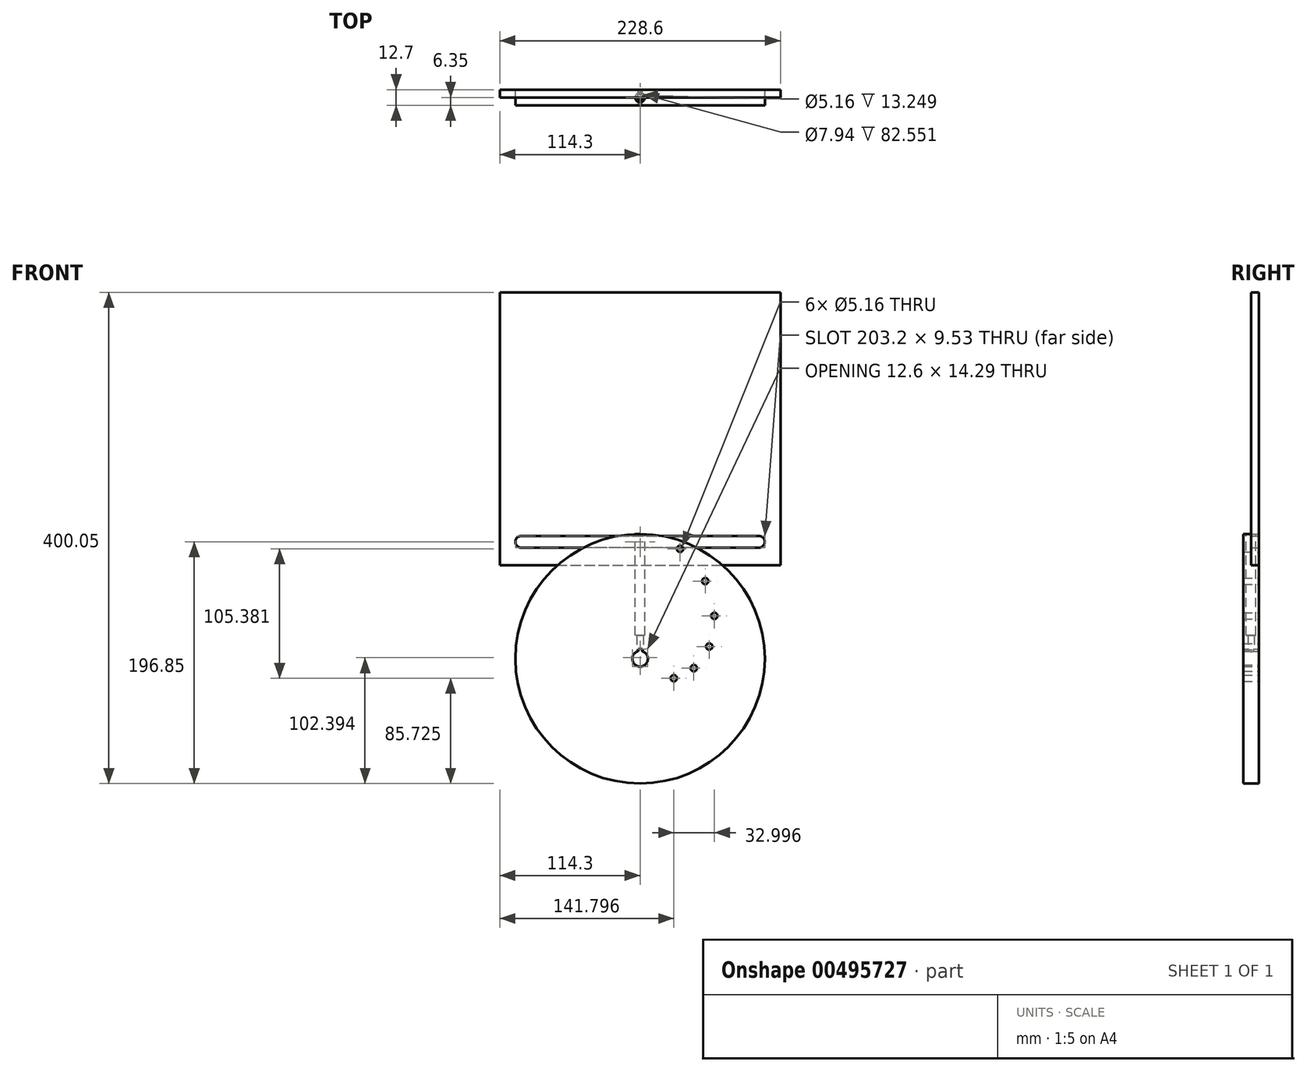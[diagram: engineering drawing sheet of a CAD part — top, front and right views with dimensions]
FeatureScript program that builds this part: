
annotation { "Feature Type Name" : "Feature", "Feature Type Description" : "" }
export const myFeature = defineFeature(function(context is Context, id is Id, definition is map)
    precondition{}
    {
        {
            var Q0;
            Q0=qCreatedBy(makeId("Front.planeOp"),FACE);
            var sketch = newSketch(context, id + "F0", { "sketchPlane" : qUnion([Q0])});
            skCircle(sketch, "E0", {"center": v(0, 0) * mm, "radius": 101.6 * mm});
            skCircle(sketch, "E1", {"center": v(0, 0) * mm, "radius": 6.35 * mm});
            skSolve(sketch);
        }
        {
            var Q0;
            Q0 = qSketchRegion(id + "F0", true);
            extrude(context, id + "F1", {"entities" : qUnion([Q0]), "depth" : 12.7 * mm});
        }
        {
            var Q0;
            Q0=qCreatedBy(makeId("Front.planeOp"),FACE);
            var sketch = newSketch(context, id + "F2", { "sketchPlane" : qUnion([Q0])});
            skLineSegment(sketch, "E2.bottom", {"start": v(-1.59, 7.94) * mm, "end": v(1.59, 7.94) * mm});
            skLineSegment(sketch, "E2.top", {"start": v(-1.59, 4.76) * mm, "end": v(1.59, 4.76) * mm});
            skLineSegment(sketch, "E2.left", {"start": v(-1.59, 7.94) * mm, "end": v(-1.59, 4.76) * mm});
            skLineSegment(sketch, "E2.right", {"start": v(1.59, 7.94) * mm, "end": v(1.59, 4.76) * mm});
            skLineSegment(sketch, "E3", {"start": v(-1.59, 7.94) * mm, "end": v(1.59, 4.76) * mm, "construction": true});
            skPoint(sketch, "E4", {"position": v(0, 6.35) * mm});
            skLineSegment(sketch, "E5", {"start": v(0, 0) * mm, "end": v(0, 9.4) * mm, "construction": true});
            skSolve(sketch);
        }
        {
            var Q0;
            Q0 = qSketchRegion(id + "F2", true);
            extrude(context, id + "F3", {"entities" : qUnion([Q0]), "operationType" : NewBodyOperationType.REMOVE, "endBound" : BoundingType.THROUGH_ALL, "depth" : 25.4 * mm});
        }
        {
            var Q0;
            Q0=qCreatedBy(makeId("Front.planeOp"),FACE);
            var sketch = newSketch(context, id + "F4", { "sketchPlane" : qUnion([Q0])});
            skCircle(sketch, "E6", {"center": v(0, 0) * mm, "radius": 95.25 * mm, "construction": true});
            skCircle(sketch, "E7", {"center": v(0, 0) * mm, "radius": 82.55 * mm, "construction": true});
            skCircle(sketch, "E8", {"center": v(0, 0) * mm, "radius": 69.85 * mm, "construction": true});
            skCircle(sketch, "E9", {"center": v(0, 0) * mm, "radius": 57.15 * mm, "construction": true});
            skCircle(sketch, "E10", {"center": v(0, 0) * mm, "radius": 44.45 * mm, "construction": true});
            skCircle(sketch, "E11", {"center": v(0, 0) * mm, "radius": 31.75 * mm, "construction": true});
            skLineSegment(sketch, "E12", {"start": v(0, 0) * mm, "end": v(29.62, 81.37) * mm, "construction": true});
            skLineSegment(sketch, "E13", {"start": v(0, 0) * mm, "end": v(57.17, 68.13) * mm, "construction": true});
            skLineSegment(sketch, "E14", {"start": v(73.08, 42.2) * mm, "end": v(0, 0) * mm, "construction": true});
            skLineSegment(sketch, "E15", {"start": v(0, 0) * mm, "end": v(83.4, 14.7) * mm, "construction": true});
            skLineSegment(sketch, "E16", {"start": v(86.7, -15.29) * mm, "end": v(0, 0) * mm, "construction": true});
            skLineSegment(sketch, "E17", {"start": v(0, 0) * mm, "end": v(78.6, -45.38) * mm, "construction": true});
            skCircle(sketch, "E18", {"center": v(32.58, 89.5) * mm, "radius": 2.58 * mm});
            skCircle(sketch, "E19", {"center": v(53.06, 63.24) * mm, "radius": 2.58 * mm});
            skCircle(sketch, "E20", {"center": v(60.5, 34.93) * mm, "radius": 2.58 * mm});
            skCircle(sketch, "E21", {"center": v(56.28, 9.92) * mm, "radius": 2.58 * mm});
            skCircle(sketch, "E22", {"center": v(43.77, -7.72) * mm, "radius": 2.58 * mm});
            skCircle(sketch, "E23", {"center": v(27.5, -15.87) * mm, "radius": 2.58 * mm});
            skLineSegment(sketch, "E24", {"start": v(0, 0) * mm, "end": v(0, 90.24) * mm, "construction": true});
            skSolve(sketch);
        }
        {
            var Q0;
            Q0 = qSketchRegion(id + "F4", true);
            extrude(context, id + "F5", {"entities" : qUnion([Q0]), "operationType" : NewBodyOperationType.REMOVE, "endBound" : BoundingType.UP_TO_NEXT, "depth" : 25.4 * mm});
        }
        {
            var Q0;
            Q0=qCreatedBy(makeId("Top.planeOp"),FACE);
            var sketch = newSketch(context, id + "F6", { "sketchPlane" : qUnion([Q0])});
            skLineSegment(sketch, "E25.0", {"start": v(101.6, -12.7) * mm, "end": v(-101.6, -12.7) * mm, "construction": true});
            skLineSegment(sketch, "E26", {"start": v(0, 0) * mm, "end": v(0, -12.7) * mm, "construction": true});
            skCircle(sketch, "E27", {"center": v(0, -6.35) * mm, "radius": 2.58 * mm});
            skSolve(sketch);
        }
        {
            var Q0;
            Q0 = qSketchRegion(id + "F6", true);
            extrude(context, id + "F7", {"entities" : qUnion([Q0]), "operationType" : NewBodyOperationType.REMOVE, "depth" : 25.4 * mm});
        }
        {
            var Q0;
            Q0=qCreatedBy(makeId("Top.planeOp"),FACE);
            cPlane(context, id + "F8", {"entities" : qUnion([Q0]), "cplaneType" : CPlaneType.OFFSET, "offset" : 152.4 * mm, "width" : 152.4 * mm, "height" : 152.4 * mm});
        }
        {
            var Q0;
            Q0=qCreatedBy(id+"F8.planeOp",FACE);
            var sketch = newSketch(context, id + "F9", { "sketchPlane" : qUnion([Q0])});
            skLineSegment(sketch, "E28.0", {"start": v(101.6, -12.7) * mm, "end": v(-101.6, -12.7) * mm, "construction": true});
            skLineSegment(sketch, "E29", {"start": v(0, 0) * mm, "end": v(0, -12.7) * mm, "construction": true});
            skCircle(sketch, "E30", {"center": v(0, -6.35) * mm, "radius": 3.97 * mm});
            skSolve(sketch);
        }
        {
            var Q0;
            Q0 = qSketchRegion(id + "F9", true);
            extrude(context, id + "F10", {"entities" : qUnion([Q0]), "operationType" : NewBodyOperationType.REMOVE, "oppositeDirection" : true, "depth" : 133.35 * mm});
        }
        {
            var Q0;
            Q0=qCreatedBy(makeId("Front.planeOp"),FACE);
            var sketch = newSketch(context, id + "F11", { "sketchPlane" : qUnion([Q0])});
            skCircle(sketch, "E31.0", {"center": v(0, 0) * mm, "radius": 101.6 * mm, "construction": true});
            skCircle(sketch, "E32", {"center": v(0, 0) * mm, "radius": 95.25 * mm, "construction": true});
            skCircle(sketch, "E33.0", {"center": v(32.58, 89.5) * mm, "radius": 2.58 * mm, "construction": true});
            skLineSegment(sketch, "E34", {"start": v(-176.1, 95.25) * mm, "end": v(199, 95.25) * mm, "construction": true});
            skLineSegment(sketch, "E35", {"start": v(-101.6, 0) * mm, "end": v(-101.6, 219.38) * mm, "construction": true});
            skLineSegment(sketch, "E36", {"start": v(101.6, 0) * mm, "end": v(101.6, 212.64) * mm, "construction": true});
            skArc(sketch, "E37", {"start": v(96.84, 90.49) * mm, "mid": v(101.6, 95.25) * mm, "end": v(96.84, 100.01) * mm});
            skArc(sketch, "E38", {"start": v(-96.84, 100.01) * mm, "mid": v(-101.6, 95.25) * mm, "end": v(-96.84, 90.49) * mm});
            skLineSegment(sketch, "E39", {"start": v(-96.84, 100.01) * mm, "end": v(96.84, 100.01) * mm});
            skLineSegment(sketch, "E40", {"start": v(96.84, 90.49) * mm, "end": v(-96.84, 90.49) * mm});
            skLineSegment(sketch, "E41.bottom", {"start": v(-114.3, 298.45) * mm, "end": v(114.3, 298.45) * mm});
            skLineSegment(sketch, "E41.top", {"start": v(-114.3, 76.2) * mm, "end": v(114.3, 76.2) * mm});
            skLineSegment(sketch, "E41.left", {"start": v(-114.3, 298.45) * mm, "end": v(-114.3, 76.2) * mm});
            skLineSegment(sketch, "E41.right", {"start": v(114.3, 298.45) * mm, "end": v(114.3, 76.2) * mm});
            skSolve(sketch);
        }
        {
            var Q0;
            Q0 = qSketchRegion(id + "F11", true);
            extrude(context, id + "F12", {"entities" : qUnion([Q0]), "depth" : 6.35 * mm});
        }
    });
